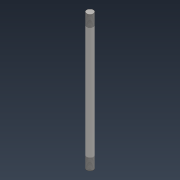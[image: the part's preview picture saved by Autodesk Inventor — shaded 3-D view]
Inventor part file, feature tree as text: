
AUTODESK INVENTOR PART (.ipt)
format: ipt  version: 2022 (Build 260153000, 153)  size: 78,848 bytes
history: native  units: mm
features: thread x2, extrude x1, sketch x1
ambient origin geometry x8: Origin, YZ Plane, XZ Plane, XY Plane, X Axis, Y Axis, Z Axis, Center Point
bodies: Solid1 (feature_tree)
feature tree (4):
  extrude  "Extrusion1"  Depth=200.0mm TaperAngle=0.0deg
  thread  "Thread1"  [1 undecoded]
  thread  "Thread2"  [1 undecoded]
  sketch  "Sketch1"  dims[d0=10.0mm d1=200.0mm d2=0.0mm d3=17.0mm d4=0.0mm d5=17.0mm d6=0.0mm]
note: 2 required parameter values undecoded (feature->parameter linkage not recoverable at this tier; creation-order binding heuristic only, values carry confidence <= 0.55)
